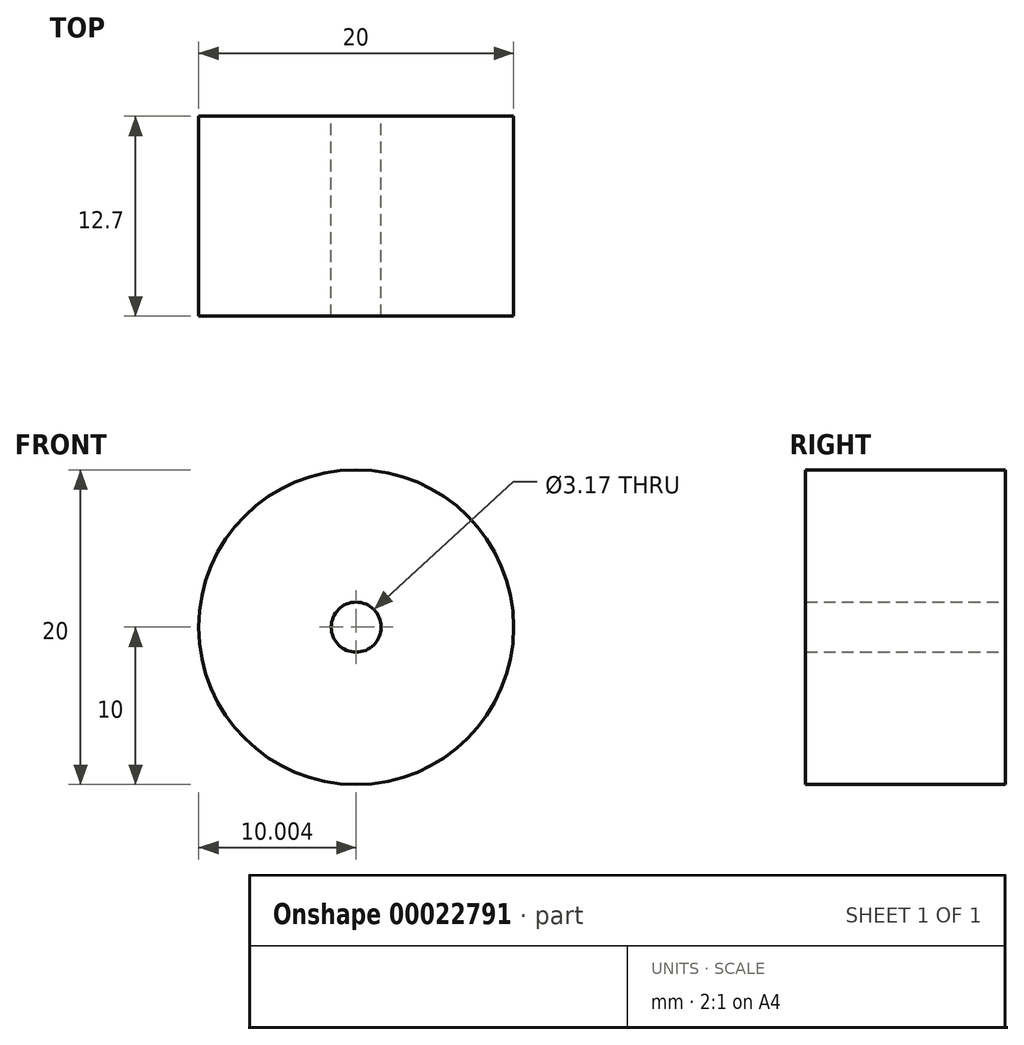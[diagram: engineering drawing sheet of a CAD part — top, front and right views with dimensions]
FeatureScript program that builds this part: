
annotation { "Feature Type Name" : "Feature", "Feature Type Description" : "" }
export const myFeature = defineFeature(function(context is Context, id is Id, definition is map)
    precondition{}
    {
        {
            var Q0;
            Q0=qCreatedBy(makeId("Front.planeOp"),FACE);
            var sketch = newSketch(context, id + "F0", { "sketchPlane" : qUnion([Q0])});
            skCircle(sketch, "E0", {"center": v(-107.72, 0) * mm, "radius": 10 * mm});
            skCircle(sketch, "E1", {"center": v(-107.72, 0) * mm, "radius": 1.59 * mm});
            skSolve(sketch);
        }
        {
            var Q0;
            Q0=makeQuery(id+"F0.imprint","IMPRINT",FACE,{"disambiguationData":[TD([[makeQuery(id+"F0.imprint","IMPRINT",EDGE,{"derivedFrom":sQuery(id+"F0.wireOp",EDGE,"E0")}),1.0]])]});
            extrude(context, id + "F1", {"entities" : qUnion([Q0]), "endBound" : BoundingType.SYMMETRIC, "depth" : 6.35 * mm});
        }
        {
            var Q0;
            Q0=makeQuery(id+"F0.imprint","IMPRINT",FACE,{"disambiguationData":[TD([[makeQuery(id+"F0.imprint","IMPRINT",EDGE,{"derivedFrom":sQuery(id+"F0.wireOp",EDGE,"E1")}),-1.0]])]});
            extrude(context, id + "F2", {"entities" : qUnion([Q0]), "operationType" : NewBodyOperationType.ADD, "endBound" : BoundingType.SYMMETRIC, "depth" : 12.7 * mm});
        }
    });
